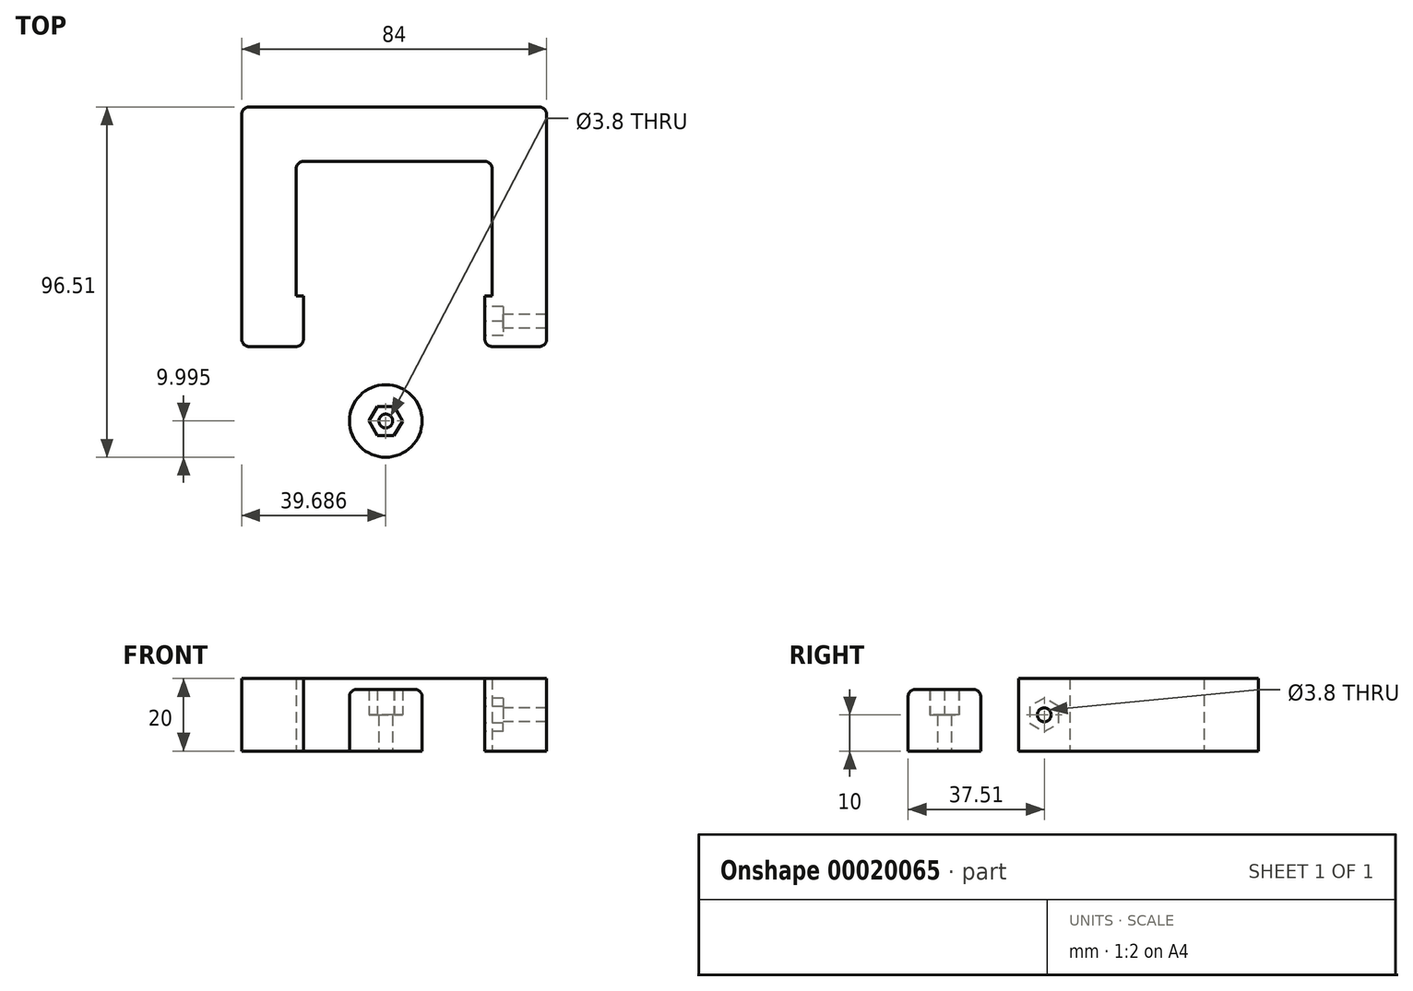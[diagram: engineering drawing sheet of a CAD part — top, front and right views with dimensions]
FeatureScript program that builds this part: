
annotation { "Feature Type Name" : "Feature", "Feature Type Description" : "" }
export const myFeature = defineFeature(function(context is Context, id is Id, definition is map)
    precondition{}
    {
        {
            var Q0;
            Q0=qCreatedBy(makeId("Top.planeOp"),FACE);
            var sketch = newSketch(context, id + "F0", { "sketchPlane" : qUnion([Q0])});
            skLineSegment(sketch, "E0.top", {"start": v(2, 40) * mm, "end": v(52, 40) * mm});
            skLineSegment(sketch, "E1.0", {"start": v(69, 2) * mm, "end": v(69, 43) * mm});
            skLineSegment(sketch, "E1.1", {"start": v(-13, 55) * mm, "end": v(57, 55) * mm});
            skPoint(sketch, "E2.visualSharp", {"position": v(-15, 55) * mm});
            skArc(sketch, "E2.filletArc", {"start": v(-13, 55) * mm, "mid": v(-14.41, 54.41) * mm, "end": v(-15, 53) * mm});
            skPoint(sketch, "E3.visualSharp", {"position": v(69, 55) * mm});
            skPoint(sketch, "E4.visualSharp", {"position": v(5, 26.5) * mm});
            skPoint(sketch, "E5.visualSharp", {"position": v(5, 33) * mm});
            skPoint(sketch, "E6.visualSharp", {"position": v(48, 33) * mm});
            skPoint(sketch, "E7.visualSharp", {"position": v(48, 26.5) * mm});
            skPoint(sketch, "E8.visualSharp", {"position": v(0, 40) * mm});
            skArc(sketch, "E8.filletArc", {"start": v(2, 40) * mm, "mid": v(0.59, 39.41) * mm, "end": v(0, 38) * mm});
            skPoint(sketch, "E9.visualSharp", {"position": v(53, 40) * mm});
            skArc(sketch, "E9.filletArc", {"start": v(54, 38) * mm, "mid": v(53.41, 39.41) * mm, "end": v(52, 40) * mm});
            skPoint(sketch, "E10.visualSharp", {"position": v(54, -11) * mm});
            skPoint(sketch, "E11.visualSharp", {"position": v(69, -11) * mm});
            skPoint(sketch, "E12.visualSharp", {"position": v(-15, -11) * mm});
            skPoint(sketch, "E13.visualSharp", {"position": v(0, 0) * mm});
            skPoint(sketch, "E14.visualSharp", {"position": v(0, 33) * mm});
            skPoint(sketch, "E15.visualSharp", {"position": v(53, 33) * mm});
            skPoint(sketch, "E16.visualSharp", {"position": v(53, 26.5) * mm});
            skPoint(sketch, "E17.visualSharp", {"position": v(0, 3) * mm});
            skLineSegment(sketch, "E18", {"start": v(54, 3) * mm, "end": v(52, 3) * mm});
            skPoint(sketch, "E19.start.orphan", {"position": v(1.85, 3) * mm});
            skLineSegment(sketch, "E20", {"start": v(0, 38) * mm, "end": v(0, 3) * mm});
            skPoint(sketch, "E21.end.orphan", {"position": v(54, 2) * mm});
            skLineSegment(sketch, "E22", {"start": v(54, 38) * mm, "end": v(54, 3) * mm});
            skLineSegment(sketch, "E23", {"start": v(57, -11) * mm, "end": v(54, -11) * mm});
            skLineSegment(sketch, "E24", {"start": v(54, -11) * mm, "end": v(52, -11) * mm});
            skLineSegment(sketch, "E25", {"start": v(52, 3) * mm, "end": v(52, -11) * mm});
            skLineSegment(sketch, "E26", {"start": v(2, 3) * mm, "end": v(0, 3) * mm});
            skPoint(sketch, "E27.end.orphan", {"position": v(50.59, 2) * mm});
            skLineSegment(sketch, "E28", {"start": v(54, -11) * mm, "end": v(69, -11) * mm});
            skLineSegment(sketch, "E29", {"start": v(69, -11) * mm, "end": v(69, 43) * mm});
            skLineSegment(sketch, "E30", {"start": v(69, 43) * mm, "end": v(69, 55) * mm});
            skLineSegment(sketch, "E31", {"start": v(69, 55) * mm, "end": v(57, 55) * mm});
            skLineSegment(sketch, "E32", {"start": v(-15, 53) * mm, "end": v(-15, -11) * mm});
            skLineSegment(sketch, "E33", {"start": v(2, -11) * mm, "end": v(-15, -11) * mm});
            skLineSegment(sketch, "E34", {"start": v(2, -11) * mm, "end": v(2, 3) * mm});
            skCircle(sketch, "E35", {"center": v(24.69, -31.51) * mm, "radius": 10 * mm});
            skCircle(sketch, "E36", {"center": v(24.69, -31.51) * mm, "radius": 1.9 * mm});
            skCircle(sketch, "E37.cCircle", {"center": v(24.69, -31.51) * mm, "radius": 4 * mm, "construction": true});
            skLineSegment(sketch, "E37.0", {"start": v(29.3, -31.56) * mm, "end": v(26.95, -35.54) * mm});
            skLineSegment(sketch, "E37.1", {"start": v(26.95, -35.54) * mm, "end": v(22.34, -35.5) * mm});
            skLineSegment(sketch, "E37.2", {"start": v(22.34, -35.5) * mm, "end": v(20.07, -31.47) * mm});
            skLineSegment(sketch, "E37.3", {"start": v(20.07, -31.47) * mm, "end": v(22.42, -27.5) * mm});
            skLineSegment(sketch, "E37.4", {"start": v(22.42, -27.5) * mm, "end": v(27.04, -27.54) * mm});
            skLineSegment(sketch, "E37.5", {"start": v(27.04, -27.54) * mm, "end": v(29.3, -31.56) * mm});
            skPoint(sketch, "E37.0.midPoint", {"position": v(28.13, -33.55) * mm});
            skSolve(sketch);
        }
        {
            var Q0;
            Q0=makeQuery(id+"F0.imprint","IMPRINT",FACE,{"disambiguationData":[TD([[makeQuery(id+"F0.imprint","IMPRINT",EDGE,{"derivedFrom":sQuery(id+"F0.wireOp",EDGE,"E0.top")}),1.0]])]});
            extrude(context, id + "F1", {"entities" : qUnion([Q0]), "depth" : 20 * mm});
        }
        {
            var Q0;
            Q0=makeQuery(id+"F1.opExtrude","SWEPT_FACE",FACE,{"disambiguationData":[OSD([sQuery(id+"F0.wireOp",EDGE,"E25")])]});
            var sketch = newSketch(context, id + "F2", { "sketchPlane" : qUnion([Q0])});
            skCircle(sketch, "E38.cCircle", {"center": v(4, 10) * mm, "radius": 4 * mm, "construction": true});
            skPoint(sketch, "E38.cCircle.centerSnap0", {"position": v(4, 20) * mm});
            skPoint(sketch, "E38.cCircle.centerSnap1", {"position": v(-3, 10) * mm});
            skLineSegment(sketch, "E38.0", {"start": v(8, 12.3) * mm, "end": v(8, 7.7) * mm});
            skLineSegment(sketch, "E38.1", {"start": v(8, 7.7) * mm, "end": v(4, 5.38) * mm});
            skLineSegment(sketch, "E38.2", {"start": v(4, 5.38) * mm, "end": v(0, 7.7) * mm});
            skLineSegment(sketch, "E38.3", {"start": v(0, 7.7) * mm, "end": v(0, 12.3) * mm});
            skLineSegment(sketch, "E38.4", {"start": v(0, 12.3) * mm, "end": v(4, 14.62) * mm});
            skLineSegment(sketch, "E38.5", {"start": v(4, 14.62) * mm, "end": v(8, 12.3) * mm});
            skPoint(sketch, "E38.0.midPoint", {"position": v(8, 10) * mm});
            skCircle(sketch, "E39", {"center": v(4, 10) * mm, "radius": 1.9 * mm});
            skSolve(sketch);
        }
        {
            var Q0;
            Q0=makeQuery(id+"F2.imprint","IMPRINT",FACE,{"disambiguationData":[TD([[makeQuery(id+"F2.imprint","IMPRINT",EDGE,{"derivedFrom":sQuery(id+"F2.wireOp",EDGE,"E39")}),1.0]])]});
            extrude(context, id + "F3", {"entities" : qUnion([Q0]), "operationType" : NewBodyOperationType.REMOVE, "oppositeDirection" : true, "depth" : 25 * mm});
        }
        {
            var Q0;
            Q0=makeQuery(id+"F2.imprint","IMPRINT",FACE,{"disambiguationData":[TD([[makeQuery(id+"F2.imprint","IMPRINT",EDGE,{"derivedFrom":sQuery(id+"F2.wireOp",EDGE,"E38.0")}),-1.0]])]});
            extrude(context, id + "F4", {"entities" : qUnion([Q0]), "operationType" : NewBodyOperationType.REMOVE, "oppositeDirection" : true, "depth" : 5 * mm});
        }
        {
            var Q0;
            Q0=makeQuery(id+"FCJR9x0iEZllUuj_1.opExtrude","CAP_EDGE",EDGE,{"disambiguationData":[OSD([sQuery(id+"F0.wireOp",EDGE,"E30"),sQuery(id+"F0.wireOp",EDGE,"E31")])],"isStart":false});
            var Q1;
            Q1=makeQuery(id+"FCJR9x0iEZllUuj_1.opExtrude","CAP_EDGE",EDGE,{"disambiguationData":[OSD([sQuery(id+"F0.wireOp",EDGE,"E28"),sQuery(id+"F0.wireOp",EDGE,"E29")])],"isStart":false});
            var Q2;
            Q2=makeQuery(id+"F1.opExtrude","SWEPT_EDGE",EDGE,{"disambiguationData":[OSD([sQuery(id+"F0.wireOp",EDGE,"E24"),sQuery(id+"F0.wireOp",EDGE,"E25")])]});
            var Q3;
            Q3=makeQuery(id+"F1.opExtrude","SWEPT_EDGE",EDGE,{"disambiguationData":[OSD([sQuery(id+"F0.wireOp",EDGE,"s2pMRHvg-Eua4-Zt46-WkjS-m37mnWGcaHP1"),sQuery(id+"F0.wireOp",EDGE,"AldMu9fZ-FfgK-HJl7-Lg6l-VCjV2pt7i5WL")])]});
            fillet(context, id + "F5", {"entities" : qUnion([Q0, Q1, Q2, Q3]), "radius" : 2 * mm, "tangentPropagation" : true, "allowEdgeOverflow" : false});
        }
        {
            var Q0;
            Q0=makeQuery(id+"F1.opExtrude","SWEPT_EDGE",EDGE,{"disambiguationData":[OSD([sQuery(id+"F0.wireOp",EDGE,"E30"),sQuery(id+"F0.wireOp",EDGE,"E31")])]});
            var Q1;
            Q1=makeQuery(id+"F1.opExtrude","SWEPT_EDGE",EDGE,{"disambiguationData":[OSD([sQuery(id+"F0.wireOp",EDGE,"E28"),sQuery(id+"F0.wireOp",EDGE,"E29")])]});
            var Q2;
            Q2=makeQuery(id+"F1.opExtrude","SWEPT_EDGE",EDGE,{"disambiguationData":[OSD([sQuery(id+"F0.wireOp",EDGE,"E33"),sQuery(id+"F0.wireOp",EDGE,"E34")])]});
            var Q3;
            Q3=makeQuery(id+"F1.opExtrude","SWEPT_EDGE",EDGE,{"disambiguationData":[OSD([sQuery(id+"F0.wireOp",EDGE,"E32"),sQuery(id+"F0.wireOp",EDGE,"E33")])]});
            fillet(context, id + "F6", {"entities" : qUnion([Q0, Q1, Q2, Q3]), "radius" : 2 * mm, "tangentPropagation" : true, "allowEdgeOverflow" : false});
        }
        {
            var Q0;
            Q0=makeQuery(id+"F0.imprint","IMPRINT",FACE,{"disambiguationData":[TD([[makeQuery(id+"F0.imprint","IMPRINT",EDGE,{"derivedFrom":sQuery(id+"F0.wireOp",EDGE,"E35")}),1.0]])]});
            extrude(context, id + "F7", {"entities" : qUnion([Q0]), "depth" : 17 * mm});
        }
        {
            var Q0;
            Q0=makeQuery(id+"F0.imprint","IMPRINT",FACE,{"disambiguationData":[TD([[makeQuery(id+"F0.imprint","IMPRINT",EDGE,{"derivedFrom":sQuery(id+"F0.wireOp",EDGE,"E36")}),-1.0]])]});
            extrude(context, id + "F8", {"entities" : qUnion([Q0]), "operationType" : NewBodyOperationType.ADD, "depth" : 10 * mm});
        }
        {
            var Q0;
            Q0=makeQuery(id+"F7.opExtrude","CAP_EDGE",EDGE,{"disambiguationData":[OSD([sQuery(id+"F0.wireOp",EDGE,"E35")])],"isStart":false});
            fillet(context, id + "F9", {"entities" : qUnion([Q0]), "radius" : 2 * mm, "tangentPropagation" : true, "allowEdgeOverflow" : false});
        }
    });
